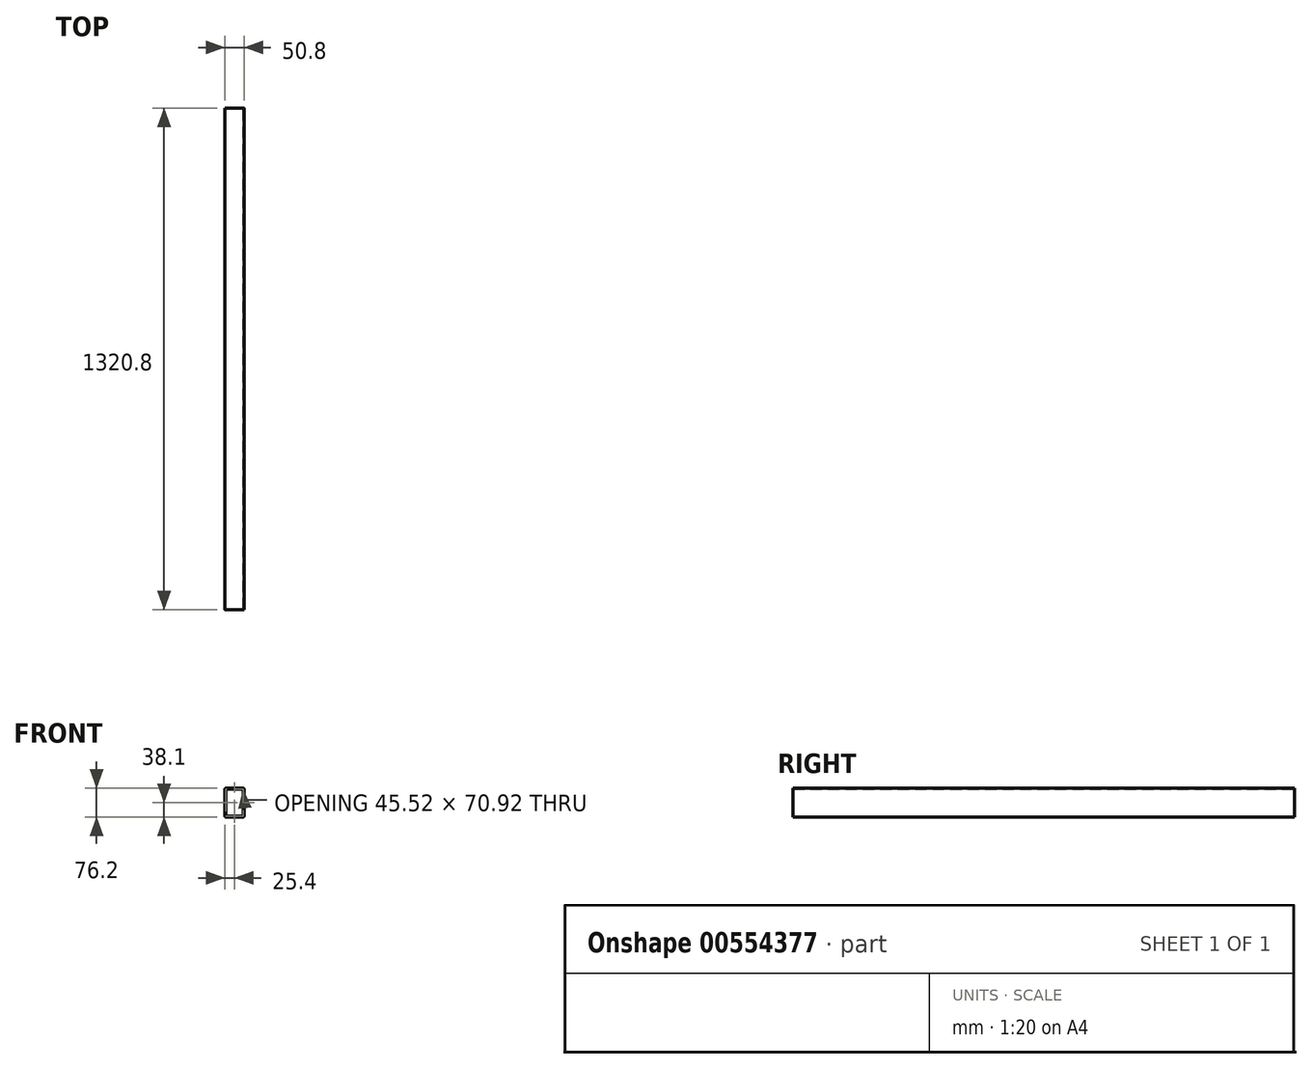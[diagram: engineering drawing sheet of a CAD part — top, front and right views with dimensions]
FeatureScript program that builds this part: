
annotation { "Feature Type Name" : "Feature", "Feature Type Description" : "" }
export const myFeature = defineFeature(function(context is Context, id is Id, definition is map)
    precondition{}
    {
        {
            var Q0;
            Q0=qCreatedBy(makeId("Front.planeOp"),FACE);
            var sketch = newSketch(context, id + "F0", { "sketchPlane" : qUnion([Q0])});
            skLineSegment(sketch, "E0.bottom", {"start": v(25.4, 38.1) * mm, "end": v(-25.4, 38.1) * mm});
            skLineSegment(sketch, "E0.top", {"start": v(25.4, -38.1) * mm, "end": v(-25.4, -38.1) * mm});
            skLineSegment(sketch, "E0.left", {"start": v(25.4, 38.1) * mm, "end": v(25.4, -38.1) * mm});
            skLineSegment(sketch, "E0.right", {"start": v(-25.4, 38.1) * mm, "end": v(-25.4, -38.1) * mm});
            skPoint(sketch, "E0.middle", {"position": v(0, 0) * mm});
            skLineSegment(sketch, "E1.bottom", {"start": v(22.76, 35.46) * mm, "end": v(-22.76, 35.46) * mm});
            skLineSegment(sketch, "E1.top", {"start": v(22.76, -35.46) * mm, "end": v(-22.76, -35.46) * mm});
            skLineSegment(sketch, "E1.left", {"start": v(22.76, 35.46) * mm, "end": v(22.76, -35.46) * mm});
            skLineSegment(sketch, "E1.right", {"start": v(-22.76, 35.46) * mm, "end": v(-22.76, -35.46) * mm});
            skSolve(sketch);
        }
        {
            var Q0;
            Q0 = qSketchRegion(id + "F0", true);
            extrude(context, id + "F1", {"entities" : qUnion([Q0]), "depth" : 1320.8 * mm, "offsetDistance" : 25.4 * mm});
        }
        {
            var Q0;
            Q0=makeQuery(id+"F1.opExtrude","SWEPT_EDGE",EDGE,{"disambiguationData":[OSD([sQuery(id+"F0.wireOp",EDGE,"E0.bottom"),sQuery(id+"F0.wireOp",EDGE,"E0.left")])]});
            var Q1;
            Q1=makeQuery(id+"F1.opExtrude","SWEPT_EDGE",EDGE,{"disambiguationData":[OSD([sQuery(id+"F0.wireOp",EDGE,"E0.bottom"),sQuery(id+"F0.wireOp",EDGE,"E0.right")])]});
            var Q2;
            Q2=makeQuery(id+"F1.opExtrude","SWEPT_EDGE",EDGE,{"disambiguationData":[OSD([sQuery(id+"F0.wireOp",EDGE,"E0.top"),sQuery(id+"F0.wireOp",EDGE,"E0.left")])]});
            var Q3;
            Q3=makeQuery(id+"F1.opExtrude","SWEPT_EDGE",EDGE,{"disambiguationData":[OSD([sQuery(id+"F0.wireOp",EDGE,"E1.top"),sQuery(id+"F0.wireOp",EDGE,"E1.right")])]});
            var Q4;
            Q4=makeQuery(id+"F1.opExtrude","SWEPT_EDGE",EDGE,{"disambiguationData":[OSD([sQuery(id+"F0.wireOp",EDGE,"E0.top"),sQuery(id+"F0.wireOp",EDGE,"E0.right")])]});
            var Q5;
            Q5=makeQuery(id+"F1.opExtrude","SWEPT_EDGE",EDGE,{"disambiguationData":[OSD([sQuery(id+"F0.wireOp",EDGE,"E1.bottom"),sQuery(id+"F0.wireOp",EDGE,"E1.left")])]});
            var Q6;
            Q6=makeQuery(id+"F1.opExtrude","SWEPT_EDGE",EDGE,{"disambiguationData":[OSD([sQuery(id+"F0.wireOp",EDGE,"E1.top"),sQuery(id+"F0.wireOp",EDGE,"E1.left")])]});
            var Q7;
            Q7=makeQuery(id+"F1.opExtrude","SWEPT_EDGE",EDGE,{"disambiguationData":[OSD([sQuery(id+"F0.wireOp",EDGE,"E1.bottom"),sQuery(id+"F0.wireOp",EDGE,"E1.right")])]});
            fillet(context, id + "F2", {"entities" : qUnion([Q0, Q1, Q2, Q3, Q4, Q5, Q6, Q7]), "radius" : 3.17 * mm, "tangentPropagation" : true, "allowEdgeOverflow" : false});
        }
    });
